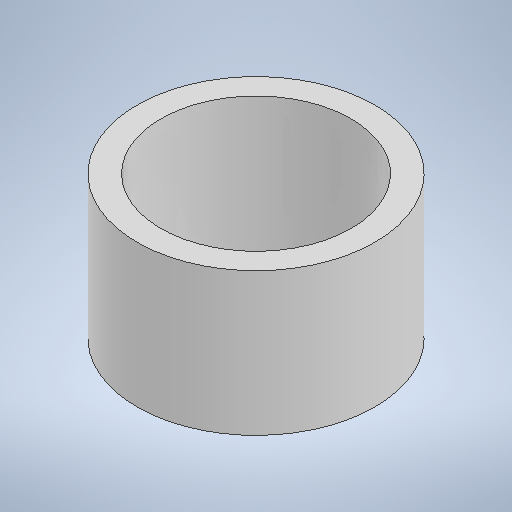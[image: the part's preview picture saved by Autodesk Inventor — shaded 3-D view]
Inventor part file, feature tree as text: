
AUTODESK INVENTOR PART (.ipt)
format: ipt  version: 2025.1 (Build 291241000, 241)  size: 259,584 bytes
history: native  units: mm
features: extrude x1, sketch x1
ambient origin geometry x8: Origin, YZ Plane, XZ Plane, XY Plane, X Axis, Y Axis, Z Axis, Center Point
bodies: Solid1 (feature_tree)
feature tree (2):
  extrude  "Extrusion1"  Depth=3.0mm
  sketch  "Sketch1"  dims[d0=5.0mm d1=4.0mm d2=3.0mm d3=0.0mm]
